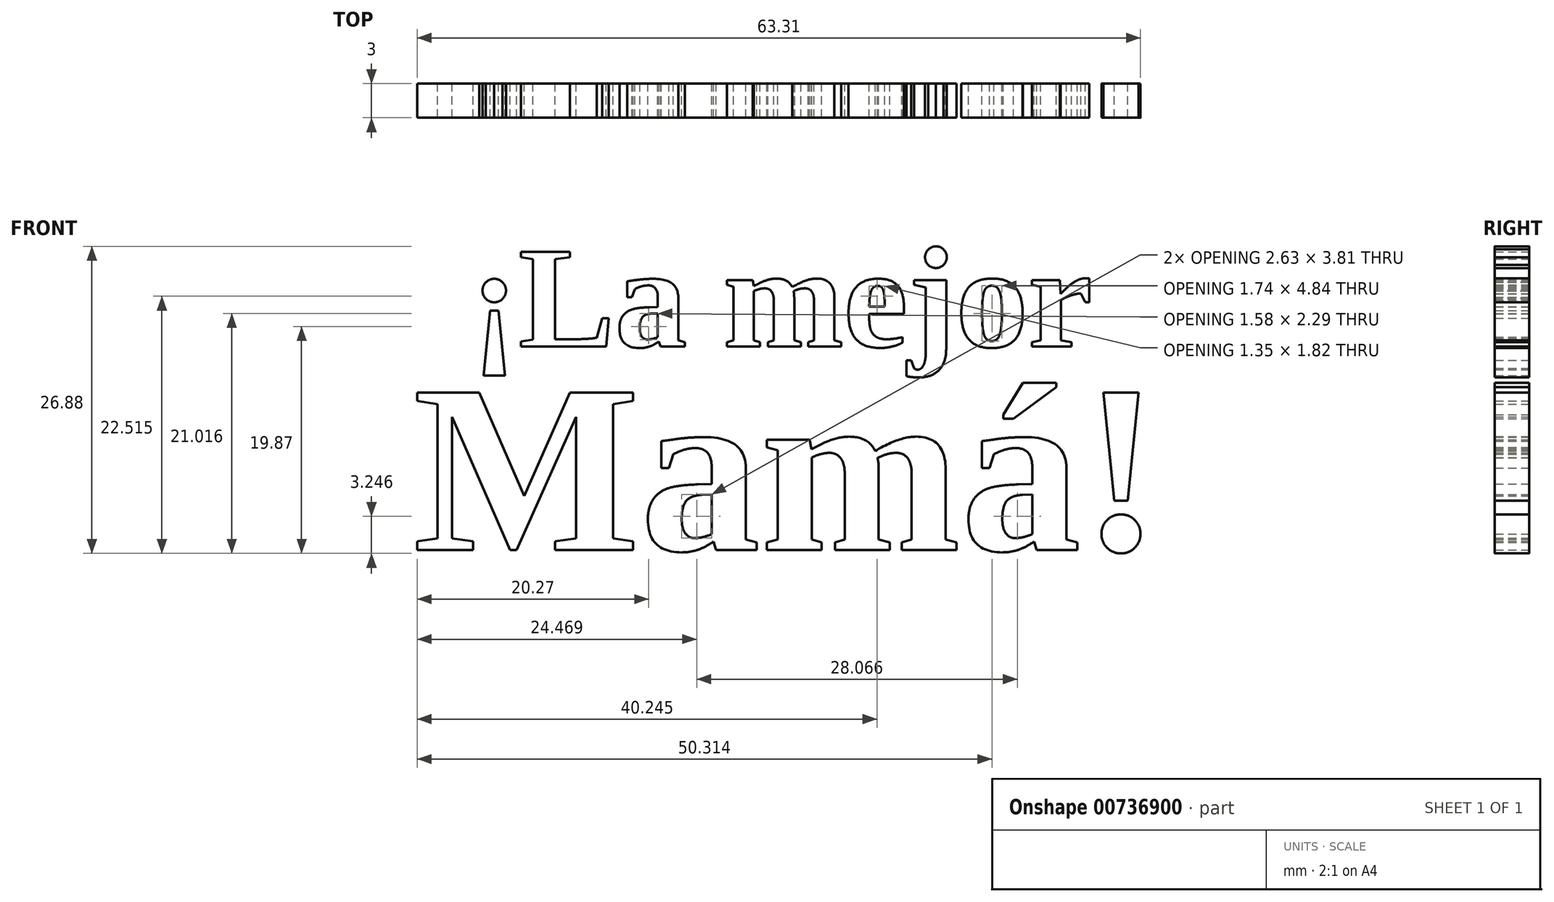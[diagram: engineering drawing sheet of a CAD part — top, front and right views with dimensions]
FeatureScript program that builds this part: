
annotation { "Feature Type Name" : "Feature", "Feature Type Description" : "" }
export const myFeature = defineFeature(function(context is Context, id is Id, definition is map)
    precondition{}
    {
        {
            var Q0;
            Q0=qCreatedBy(makeId("Front.planeOp"),FACE);
            var sketch = newSketch(context, id + "F0", { "sketchPlane" : qUnion([Q0])});
            skText(sketch, "E0", { "text": "Mamá!", "fontName": "Tinos-Bold.ttf"});
            skText(sketch, "E1", { "text": "¡La mejor", "fontName": "Tinos-Bold.ttf"});
            const initialGuessF0  = {"E0": [-0.0325, -0.02233, 1, 0, 0.01516], "E1": [-0.0275, -0.00453, 1, 0, 0.00911]};
            skSetInitialGuess(sketch, initialGuessF0);
            skSolve(sketch);
        }
        {
            var Q0;
            Q0 = qSketchRegion(id + "F0", true);
            var Q1;
            Q1=makeQuery(id+"F0.imprint","IMPRINT",FACE,{"disambiguationData":[TD([[makeQuery(id+"F0.imprint","IMPRINT",EDGE,{"derivedFrom":sQuery(id+"F0.wireOp",EDGE,"E0.sketch_text.stroke-25")}),-1.0]])]});
            var Q2;
            Q2=makeQuery(id+"F0.imprint","IMPRINT",FACE,{"disambiguationData":[TD([[makeQuery(id+"F0.imprint","IMPRINT",EDGE,{"derivedFrom":sQuery(id+"F0.wireOp",EDGE,"E0.sketch_text.stroke-90")}),-1.0]])]});
            var Q3;
            Q3=makeQuery(id+"F0.imprint","IMPRINT",FACE,{"disambiguationData":[TD([[makeQuery(id+"F0.imprint","IMPRINT",EDGE,{"derivedFrom":sQuery(id+"F0.wireOp",EDGE,"E0.sketch_text.stroke-0")}),-1.0]])]});
            var Q4;
            Q4=makeQuery(id+"F0.imprint","IMPRINT",FACE,{"disambiguationData":[TD([[makeQuery(id+"F0.imprint","IMPRINT",EDGE,{"derivedFrom":sQuery(id+"F0.wireOp",EDGE,"E0.sketch_text.stroke-53")}),-1.0]])]});
            var Q5;
            Q5=makeQuery(id+"F0.imprint","IMPRINT",FACE,{"disambiguationData":[TD([[makeQuery(id+"F0.imprint","IMPRINT",EDGE,{"derivedFrom":sQuery(id+"F0.wireOp",EDGE,"E0.sketch_text.stroke-118")}),-1.0]])]});
            var Q6;
            Q6=makeQuery(id+"F0.imprint","IMPRINT",FACE,{"disambiguationData":[TD([[makeQuery(id+"F0.imprint","IMPRINT",EDGE,{"derivedFrom":sQuery(id+"F0.wireOp",EDGE,"E0.sketch_text.stroke-124")}),-1.0]])]});
            var Q7;
            Q7=makeQuery(id+"F0.imprint","IMPRINT",FACE,{"disambiguationData":[TD([[makeQuery(id+"F0.imprint","IMPRINT",EDGE,{"derivedFrom":sQuery(id+"F0.wireOp",EDGE,"E1.sketch_text.stroke-27")}),-1.0]])]});
            var Q8;
            Q8=makeQuery(id+"F0.imprint","IMPRINT",FACE,{"disambiguationData":[TD([[makeQuery(id+"F0.imprint","IMPRINT",EDGE,{"derivedFrom":sQuery(id+"F0.wireOp",EDGE,"E0.sketch_text.stroke-128")}),-1.0]])]});
            var Q9;
            Q9=makeQuery(id+"F0.imprint","IMPRINT",FACE,{"disambiguationData":[TD([[makeQuery(id+"F0.imprint","IMPRINT",EDGE,{"derivedFrom":sQuery(id+"F0.wireOp",EDGE,"E1.sketch_text.stroke-0")}),-1.0]])]});
            var Q10;
            Q10=makeQuery(id+"F0.imprint","IMPRINT",FACE,{"disambiguationData":[TD([[makeQuery(id+"F0.imprint","IMPRINT",EDGE,{"derivedFrom":sQuery(id+"F0.wireOp",EDGE,"E1.sketch_text.stroke-92")}),-1.0]])]});
            var Q11;
            Q11=makeQuery(id+"F0.imprint","IMPRINT",FACE,{"disambiguationData":[TD([[makeQuery(id+"F0.imprint","IMPRINT",EDGE,{"derivedFrom":sQuery(id+"F0.wireOp",EDGE,"E1.sketch_text.stroke-4")}),-1.0]])]});
            var Q12;
            Q12=makeQuery(id+"F0.imprint","IMPRINT",FACE,{"disambiguationData":[TD([[makeQuery(id+"F0.imprint","IMPRINT",EDGE,{"derivedFrom":sQuery(id+"F0.wireOp",EDGE,"E1.sketch_text.stroke-12")}),-1.0]])]});
            var Q13;
            Q13=makeQuery(id+"F0.imprint","IMPRINT",FACE,{"disambiguationData":[TD([[makeQuery(id+"F0.imprint","IMPRINT",EDGE,{"derivedFrom":sQuery(id+"F0.wireOp",EDGE,"E1.sketch_text.stroke-114")}),-1.0]])]});
            var Q14;
            Q14=makeQuery(id+"F0.imprint","IMPRINT",FACE,{"disambiguationData":[TD([[makeQuery(id+"F0.imprint","IMPRINT",EDGE,{"derivedFrom":sQuery(id+"F0.wireOp",EDGE,"E1.sketch_text.stroke-122")}),-1.0]])]});
            var Q15;
            Q15=makeQuery(id+"F0.imprint","IMPRINT",FACE,{"disambiguationData":[TD([[makeQuery(id+"F0.imprint","IMPRINT",EDGE,{"derivedFrom":sQuery(id+"F0.wireOp",EDGE,"E1.sketch_text.stroke-136")}),-1.0]])]});
            var Q16;
            Q16=makeQuery(id+"F0.imprint","IMPRINT",FACE,{"disambiguationData":[TD([[makeQuery(id+"F0.imprint","IMPRINT",EDGE,{"derivedFrom":sQuery(id+"F0.wireOp",EDGE,"E1.sketch_text.stroke-152")}),-1.0]])]});
            var Q17;
            Q17=makeQuery(id+"F0.imprint","IMPRINT",FACE,{"disambiguationData":[TD([[makeQuery(id+"F0.imprint","IMPRINT",EDGE,{"derivedFrom":sQuery(id+"F0.wireOp",EDGE,"E1.sketch_text.stroke-55")}),-1.0]])]});
            extrude(context, id + "F1", {"entities" : qUnion([Q0, Q1, Q2, Q3, Q4, Q5, Q6, Q7, Q8, Q9, Q10, Q11, Q12, Q13, Q14, Q15, Q16, Q17]), "depth" : 3 * mm, "offsetDistance" : 25 * mm});
        }
    });
